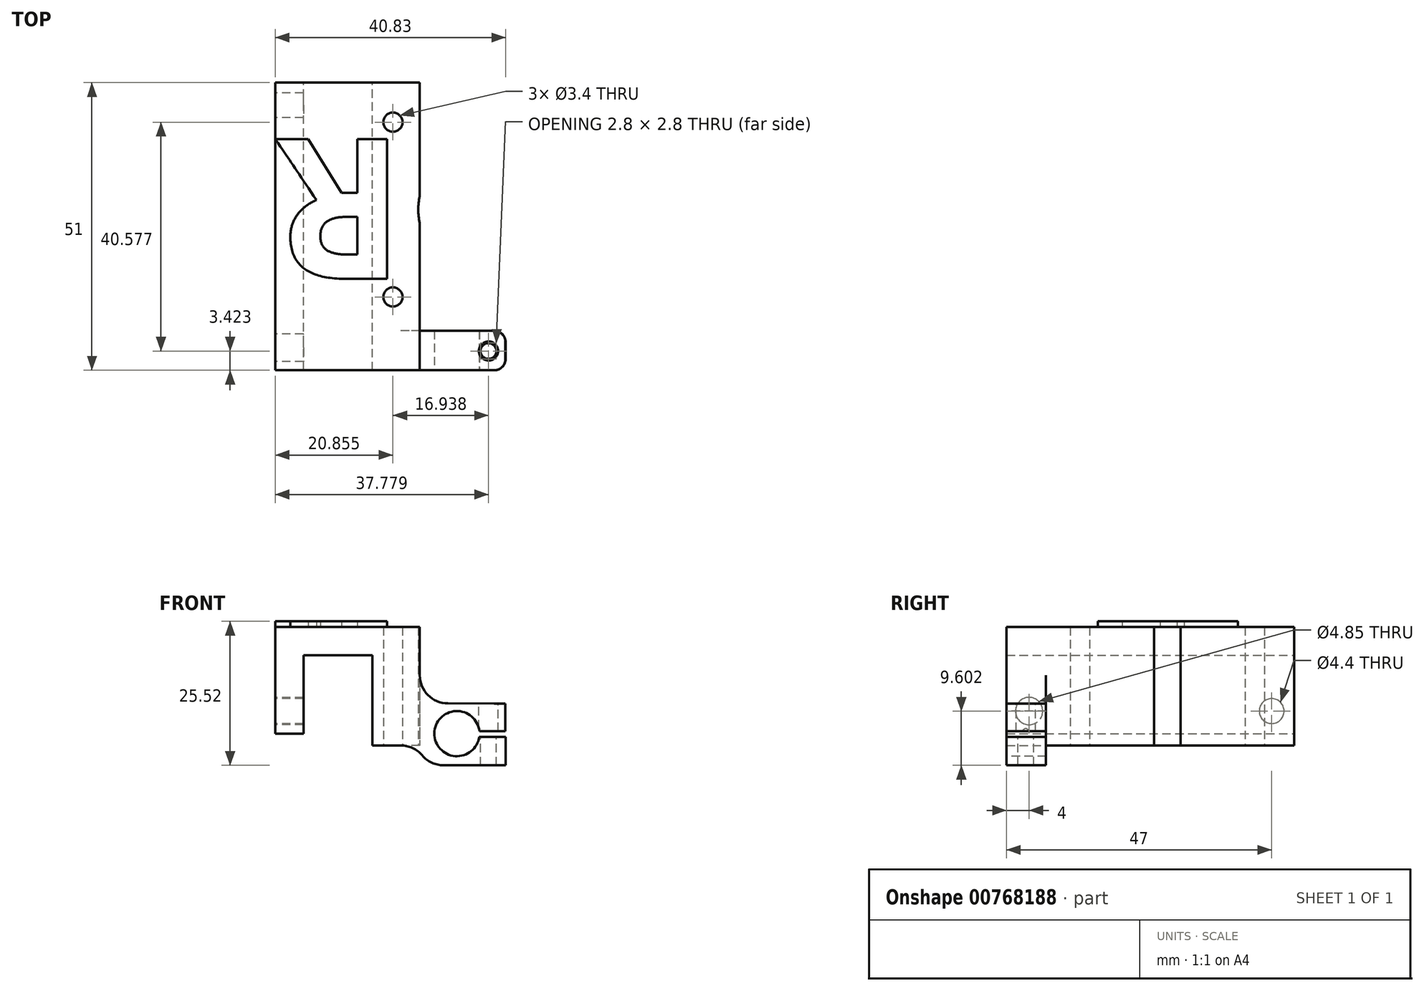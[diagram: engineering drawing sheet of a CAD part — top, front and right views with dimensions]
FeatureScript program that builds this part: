
annotation { "Feature Type Name" : "Feature", "Feature Type Description" : "" }
export const myFeature = defineFeature(function(context is Context, id is Id, definition is map)
    precondition{}
    {
        {
            var Q0;
            Q0=qCreatedBy(makeId("Front.planeOp"),FACE);
            var sketch = newSketch(context, id + "F0", { "sketchPlane" : qUnion([Q0])});
            skLineSegment(sketch, "E0", {"start": v(-18.67, 10.9) * mm, "end": v(-18.67, 29.8) * mm});
            skLineSegment(sketch, "E1", {"start": v(-18.67, 29.8) * mm, "end": v(6.94, 29.8) * mm});
            skLineSegment(sketch, "E2", {"start": v(6.94, 29.8) * mm, "end": v(6.94, 16.27) * mm});
            skLineSegment(sketch, "E3", {"start": v(-1.47, 8.8) * mm, "end": v(-1.47, 24.8) * mm});
            skLineSegment(sketch, "E4", {"start": v(-1.47, 24.8) * mm, "end": v(-13.67, 24.8) * mm});
            skLineSegment(sketch, "E5", {"start": v(-13.67, 24.8) * mm, "end": v(-13.67, 10.9) * mm});
            skLineSegment(sketch, "E6", {"start": v(-13.67, 10.9) * mm, "end": v(-18.67, 10.9) * mm});
            skLineSegment(sketch, "E7", {"start": v(6.94, 16.27) * mm, "end": v(6.94, 8.8) * mm});
            skLineSegment(sketch, "E8", {"start": v(6.94, 8.8) * mm, "end": v(-1.47, 8.8) * mm});
            skLineSegment(sketch, "E9", {"start": v(6.94, 16.27) * mm, "end": v(6.94, 16.27) * mm});
            skLineSegment(sketch, "E10", {"start": v(22.13, 16.24) * mm, "end": v(22.13, 11.34) * mm});
            skLineSegment(sketch, "E11", {"start": v(22.13, 11.34) * mm, "end": v(15.49, 11.34) * mm});
            skLineSegment(sketch, "E12", {"start": v(15.49, 11.34) * mm, "end": v(15.49, 10.34) * mm});
            skLineSegment(sketch, "E13", {"start": v(15.49, 10.34) * mm, "end": v(22.16, 10.34) * mm});
            skLineSegment(sketch, "E14", {"start": v(22.16, 10.34) * mm, "end": v(22.16, 5.29) * mm});
            skLineSegment(sketch, "E15", {"start": v(22.16, 5.29) * mm, "end": v(8.35, 5.29) * mm});
            skLineSegment(sketch, "E16", {"start": v(8.35, 5.29) * mm, "end": v(6.94, 8.8) * mm});
            skLineSegment(sketch, "E17", {"start": v(22.13, 16.24) * mm, "end": v(6.94, 16.27) * mm});
            skSolve(sketch);
        }
        {
            var Q0;
            Q0=makeQuery(id+"F0.imprint","IMPRINT",FACE,{"disambiguationData":[TD([[makeQuery(id+"F0.imprint","IMPRINT",EDGE,{"derivedFrom":sQuery(id+"F0.wireOp",EDGE,"E0")}),-1.0]])]});
            var Q1;
            {var subQ2=sQuery(id+"F0.wireOp",EDGE,"69cbcc5d-e0c3-48db-8baf-3487a8abab7d");Q1=makeQuery(id+"F0.imprint","IMPRINT",FACE,{"disambiguationData":[TD([[makeQuery(id+"F0.imprint","IMPRINT",EDGE,{"derivedFrom":subQ2}),-1.0]])]});}
            var Q2;
            Q2=makeQuery(id+"F0.imprint","IMPRINT",FACE,{"disambiguationData":[TD([[makeQuery(id+"F0.imprint","IMPRINT",EDGE,{"derivedFrom":sQuery(id+"F0.wireOp",EDGE,"E7")}),1.0]])]});
            extrude(context, id + "F1", {"entities" : qUnion([Q0, Q1, Q2]), "depth" : 7 * mm});
        }
        {
            var Q0;
            Q0=makeQuery(id+"F0.imprint","IMPRINT",FACE,{"disambiguationData":[TD([[makeQuery(id+"F0.imprint","IMPRINT",EDGE,{"derivedFrom":sQuery(id+"F0.wireOp",EDGE,"E0")}),-1.0]])]});
            extrude(context, id + "F2", {"entities" : qUnion([Q0]), "operationType" : NewBodyOperationType.ADD, "oppositeDirection" : true, "depth" : 44 * mm, "offsetDistance" : 25 * mm});
        }
        {
            var Q0;
            {var subQ0=sQuery(id+"F0.wireOp",EDGE,"E8");Q0=makeQuery(id+"F2.boolean.opBoolean","MERGE",FACE,{"derivedFrom":[makeQuery(id+"F1.opExtrude","SWEPT_FACE",FACE,{"disambiguationData":[OSD([subQ0])]}),makeQuery(id+"F2.opExtrude","SWEPT_FACE",FACE,{"disambiguationData":[OSD([subQ0])]})]});}
            var sketch = newSketch(context, id + "F3", { "sketchPlane" : qUnion([Q0])});
            skCircle(sketch, "E18", {"center": v(2.19, -6) * mm, "radius": 1.7 * mm});
            skCircle(sketch, "E19", {"center": v(2.19, -37) * mm, "radius": 1.7 * mm});
            skCircle(sketch, "E20", {"center": v(17.69, -21.5) * mm, "radius": 11 * mm});
            skSolve(sketch);
        }
        {
            var Q0;
            Q0=qSketchRegion(id+"F3",true);
            extrude(context, id + "F4", {"entities" : qUnion([Q0]), "operationType" : NewBodyOperationType.REMOVE, "endBound" : BoundingType.THROUGH_ALL, "oppositeDirection" : true, "depth" : 25 * mm});
        }
        {
            var Q0;
            Q0=makeQuery(id+"F1.opExtrude","CAP_FACE",FACE,{"disambiguationData":[OSD([sQuery(id+"F0.wireOp",EDGE,"E0"),sQuery(id+"F0.wireOp",EDGE,"E1"),sQuery(id+"F0.wireOp",EDGE,"E2"),sQuery(id+"F0.wireOp",EDGE,"E3"),sQuery(id+"F0.wireOp",EDGE,"E4"),sQuery(id+"F0.wireOp",EDGE,"E5"),sQuery(id+"F0.wireOp",EDGE,"E6"),sQuery(id+"F0.wireOp",EDGE,"E8"),sQuery(id+"F0.wireOp",EDGE,"E9"),sQuery(id+"F0.wireOp",EDGE,"58f11638-63e7-4b32-8aff-a1ba3c53649b"),sQuery(id+"F0.wireOp",EDGE,"E10"),sQuery(id+"F0.wireOp",EDGE,"E11"),sQuery(id+"F0.wireOp",EDGE,"E12"),sQuery(id+"F0.wireOp",EDGE,"E13"),sQuery(id+"F0.wireOp",EDGE,"E14"),sQuery(id+"F0.wireOp",EDGE,"E15"),sQuery(id+"F0.wireOp",EDGE,"E16")])],"isStart":false});
            var sketch = newSketch(context, id + "F5", { "sketchPlane" : qUnion([Q0])});
            skCircle(sketch, "E21", {"center": v(13.53, 10.9) * mm, "radius": 4 * mm});
            skSolve(sketch);
        }
        {
            var Q0;
            Q0=qSketchRegion(id+"F5",true);
            extrude(context, id + "F6", {"entities" : qUnion([Q0]), "operationType" : NewBodyOperationType.REMOVE, "oppositeDirection" : true, "depth" : 10 * mm});
        }
        {
            var Q0;
            Q0=qSketchRegion(id+"F3",true);
            extrude(context, id + "F7", {"entities" : qUnion([Q0]), "operationType" : NewBodyOperationType.REMOVE, "endBound" : BoundingType.THROUGH_ALL, "oppositeDirection" : true, "depth" : 25 * mm});
        }
        {
            var Q0;
            Q0=makeQuery(id+"F1.opExtrude","SWEPT_FACE",FACE,{"disambiguationData":[OSD([sQuery(id+"F0.wireOp",EDGE,"E17")])]});
            var sketch = newSketch(context, id + "F8", { "sketchPlane" : qUnion([Q0])});
            skCircle(sketch, "E22", {"center": v(19.1, -3.58) * mm, "radius": 1.7 * mm});
            skCircle(sketch, "E23", {"center": v(19.1, -3.58) * mm, "radius": 1.4 * mm});
            skSolve(sketch);
        }
        {
            var Q0;
            Q0=makeQuery(id+"F8.imprint","IMPRINT",FACE,{"disambiguationData":[TD([[makeQuery(id+"F8.imprint","IMPRINT",EDGE,{"derivedFrom":sQuery(id+"F8.wireOp",EDGE,"E23")}),1.0]])]});
            extrude(context, id + "F9", {"entities" : qUnion([Q0]), "operationType" : NewBodyOperationType.REMOVE, "endBound" : BoundingType.THROUGH_ALL, "oppositeDirection" : true, "depth" : 25 * mm});
        }
        {
            var Q0;
            Q0=makeQuery(id+"F8.imprint","IMPRINT",FACE,{"disambiguationData":[TD([[makeQuery(id+"F8.imprint","IMPRINT",EDGE,{"derivedFrom":sQuery(id+"F8.wireOp",EDGE,"E22")}),1.0]])]});
            extrude(context, id + "F10", {"entities" : qUnion([Q0]), "operationType" : NewBodyOperationType.REMOVE, "endBound" : BoundingType.UP_TO_NEXT, "oppositeDirection" : true, "depth" : 25 * mm});
        }
        {
            var Q0;
            Q0=makeQuery(id+"F1.opExtrude","SWEPT_EDGE",EDGE,{"disambiguationData":[OSD([sQuery(id+"F0.wireOp",EDGE,"E2"),sQuery(id+"F0.wireOp",EDGE,"E7"),sQuery(id+"F0.wireOp",EDGE,"E17")])]});
            fillet(context, id + "F11", {"entities" : qUnion([Q0]), "radius" : 5 * mm, "tangentPropagation" : true, "allowEdgeOverflow" : false});
        }
        {
            var Q0;
            Q0=makeQuery(id+"F1.opExtrude","SWEPT_EDGE",EDGE,{"disambiguationData":[OSD([sQuery(id+"F0.wireOp",EDGE,"E7"),sQuery(id+"F0.wireOp",EDGE,"E8"),sQuery(id+"F0.wireOp",EDGE,"E16")])]});
            fillet(context, id + "F12", {"entities" : qUnion([Q0]), "radius" : 5 * mm, "tangentPropagation" : true, "allowEdgeOverflow" : false});
        }
        {
            var Q0;
            Q0=makeQuery(id+"F1.opExtrude","SWEPT_EDGE",EDGE,{"disambiguationData":[OSD([sQuery(id+"F0.wireOp",EDGE,"E15"),sQuery(id+"F0.wireOp",EDGE,"E16")])]});
            fillet(context, id + "F13", {"entities" : qUnion([Q0]), "radius" : 5 * mm, "tangentPropagation" : true, "allowEdgeOverflow" : false});
        }
        {
            var Q0;
            Q0=makeQuery(id+"F1.opExtrude","CAP_EDGE",EDGE,{"disambiguationData":[OSD([sQuery(id+"F0.wireOp",EDGE,"E10")])],"isStart":false});
            var Q1;
            Q1=makeQuery(id+"F1.opExtrude","CAP_EDGE",EDGE,{"disambiguationData":[OSD([sQuery(id+"F0.wireOp",EDGE,"E14")])],"isStart":false});
            var Q2;
            Q2=makeQuery(id+"F1.opExtrude","CAP_EDGE",EDGE,{"disambiguationData":[OSD([sQuery(id+"F0.wireOp",EDGE,"E10")])],"isStart":true});
            var Q3;
            Q3=makeQuery(id+"F1.opExtrude","CAP_EDGE",EDGE,{"disambiguationData":[OSD([sQuery(id+"F0.wireOp",EDGE,"E14")])],"isStart":true});
            fillet(context, id + "F14", {"entities" : qUnion([Q0, Q1, Q2, Q3]), "radius" : 2 * mm, "tangentPropagation" : true, "allowEdgeOverflow" : false});
        }
        {
            var Q0;
            {var subQ0=sQuery(id+"F0.wireOp",EDGE,"E0");Q0=makeQuery(id+"F2.boolean.opBoolean","MERGE",FACE,{"derivedFrom":[makeQuery(id+"F1.opExtrude","SWEPT_FACE",FACE,{"disambiguationData":[OSD([subQ0])]}),makeQuery(id+"F2.opExtrude","SWEPT_FACE",FACE,{"disambiguationData":[OSD([subQ0])]})]});}
            var sketch = newSketch(context, id + "F15", { "sketchPlane" : qUnion([Q0])});
            skCircle(sketch, "E24", {"center": v(-40, 14.9) * mm, "radius": 2.2 * mm});
            skCircle(sketch, "E25", {"center": v(3, 14.9) * mm, "radius": 2.43 * mm});
            skSolve(sketch);
        }
        {
            var Q0;
            Q0=qSketchRegion(id+"F15",true);
            extrude(context, id + "F16", {"entities" : qUnion([Q0]), "operationType" : NewBodyOperationType.REMOVE, "oppositeDirection" : true, "depth" : 6 * mm});
        }
        {
            var Q0;
            {var subQ0=sQuery(id+"F0.wireOp",EDGE,"E1");Q0=makeQuery(id+"F2.boolean.opBoolean","MERGE",FACE,{"derivedFrom":[makeQuery(id+"F1.opExtrude","SWEPT_FACE",FACE,{"disambiguationData":[OSD([subQ0])]}),makeQuery(id+"F2.opExtrude","SWEPT_FACE",FACE,{"disambiguationData":[OSD([subQ0])]})]});}
            var sketch = newSketch(context, id + "F17", { "sketchPlane" : qUnion([Q0])});
            skText(sketch, "E26", { "text": "R", "fontName": "OpenSans-Bold.ttf"});
            skPoint(sketch, "E27", {"position": v(4.25, 21.5) * mm});
            skLineSegment(sketch, "E28", {"start": v(2.19, 6) * mm, "end": v(2.19, 37) * mm, "construction": true});
            skPoint(sketch, "E29", {"position": v(2.19, 21.5) * mm});
            const initialGuessF17  = {"E26": [0.00425, 0.034, -1, 0, 0.025]};
            skSetInitialGuess(sketch, initialGuessF17);
            skSolve(sketch);
        }
        {
            var Q0;
            Q0=qSketchRegion(id+"F17",true);
            extrude(context, id + "F18", {"entities" : qUnion([Q0]), "operationType" : NewBodyOperationType.ADD, "depth" : 1 * mm});
        }
    });
